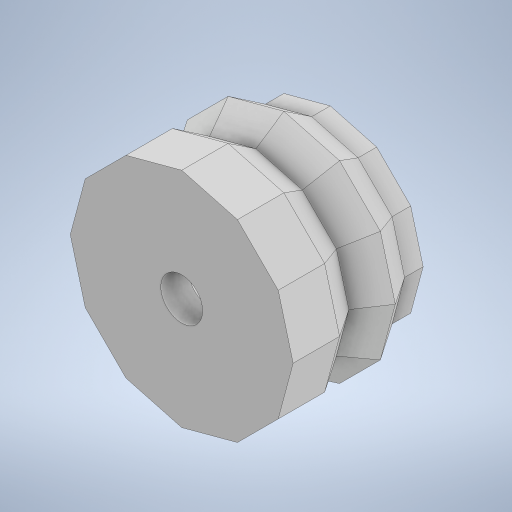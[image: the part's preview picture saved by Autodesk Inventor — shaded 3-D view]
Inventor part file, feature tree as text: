
AUTODESK INVENTOR PART (.ipt)
format: ipt  version: 2023 (Build 270158000, 158)  size: 362,496 bytes
history: native  units: in
note: dims shown in document units (in); Inventor stores cm internally (conversion verified against a paired STEP export)
features: sketch x6, extrude x4, projected_geometry x3, other x2, mirror x2, loft x1, shell x1
ambient origin geometry x8: Origin, YZ Plane, XZ Plane, XY Plane, X Axis, Y Axis, Z Axis, Center Point
bodies: Body1 (feature_tree)
feature tree (19):
  other  "솔리드1"
  sketch  "스케치1"
  other  "작업 평면1"
  loft  "로프트1"
  mirror  "미러1"
  mirror  "미러2"
  extrude  "돌출1"  Depth=0.1181in
  shell  "쉘1"  Thickness=0.7874in
  extrude  "돌출2"  TaperAngle=0.0deg  [1 undecoded]
  extrude  "돌출3"  TaperAngle=0.0deg  [1 undecoded]
  extrude  "돌출4"  Depth=0.0984in TaperAngle=0.0deg
  sketch  "스케치2"
  sketch  "스케치3"
  projected_geometry  "투영된 루프1"
  sketch  "스케치4"
  projected_geometry  "투영된 루프2"
  sketch  "스케치5"
  sketch  "스케치6"
  projected_geometry  "투영된 루프3"
note: 2 required parameter values undecoded (feature->parameter linkage not recoverable at this tier; creation-order binding heuristic only, values carry confidence <= 0.55)
